# Revit family: Kal_A3-Aluminium-Sliding-Single-sidelights+fan
name_source: partatom
category: Doors
revit_build: Autodesk Revit 2016 (Build: 20150220_1215(x64)
units: mm (PartAtom-declared; Revit-internal decimal feet)

## family parameters
Always vertical = Yes
Cut with Voids When Loaded = No
Host = Wall
Room Calculation Point = No
Shared = No

## types (8) — shared parameters
Construction Type = Aluminium
Frame Finish = Anodised Aluminium
Function = Interior
Manufacturer = Kal-Aluminium
Material Door Frame = Default Aluminium Door Frame
Material Glass = Glass
Model = Arcadia Patio Doors
Model Type = Single Sliding
URL = http://www.kal.co.za
Wall Closure = By host
zero-valued in all types: Rough Height, Rough Width, Thickness

## per-type parameters (varying)
| type | Height | Width | dh | dw | fh | ww |
| 1800 & 600 sidelights | 2550 mm  [stored 8.36614 ft] | 3000 mm  [stored 9.84252 ft] | 2125 mm | 1800 mm  [stored 5.90551 ft] | 425 mm  [stored 1.39436 ft] | 600 mm |
| 1800 & 900 sidelights | 2725 mm  [stored 8.94029 ft] | 3600 mm  [stored 11.811 ft] | 2125 mm | 1800 mm  [stored 5.90551 ft] | 600 mm | 900 mm  [stored 2.95276 ft] |
| 2100 X 600 sidelights | 2805 mm  [stored 9.20276 ft] | 3300 mm  [stored 10.8268 ft] | 2125 mm | 2100 mm | 680 mm  [stored 2.23097 ft] | 600 mm |
| 2100 X 900 sidelights | 2725 mm  [stored 8.94029 ft] | 3900 mm  [stored 12.7953 ft] | 2125 mm | 2100 mm | 600 mm | 900 mm  [stored 2.95276 ft] |
| 2400 X 600 sidelights | 2725 mm  [stored 8.94029 ft] | 3600 mm  [stored 11.811 ft] | 2125 mm | 2400 mm | 600 mm | 600 mm |
| 2400 X 900 sidelights | 3065 mm  [stored 10.0558 ft] | 4200 mm | 2465 mm  [stored 8.08727 ft] | 2400 mm | 600 mm | 900 mm  [stored 2.95276 ft] |
| 1500 X 600 sidelights | 2725 mm  [stored 8.94029 ft] | 2700 mm  [stored 8.85827 ft] | 2125 mm | 1500 mm  [stored 4.92126 ft] | 600 mm | 600 mm |
| 1500 X 900 sidelights | 2725 mm  [stored 8.94029 ft] | 3300 mm  [stored 10.8268 ft] | 2125 mm | 1500 mm  [stored 4.92126 ft] | 600 mm | 900 mm  [stored 2.95276 ft] |

note: [stored X ft] marks values corroborated as IEEE doubles in the binary element streams (Revit-internal decimal feet)

## geometry (parser evidence)
native form markers: Sweep x6
no freeform markers — native parametric forms only
